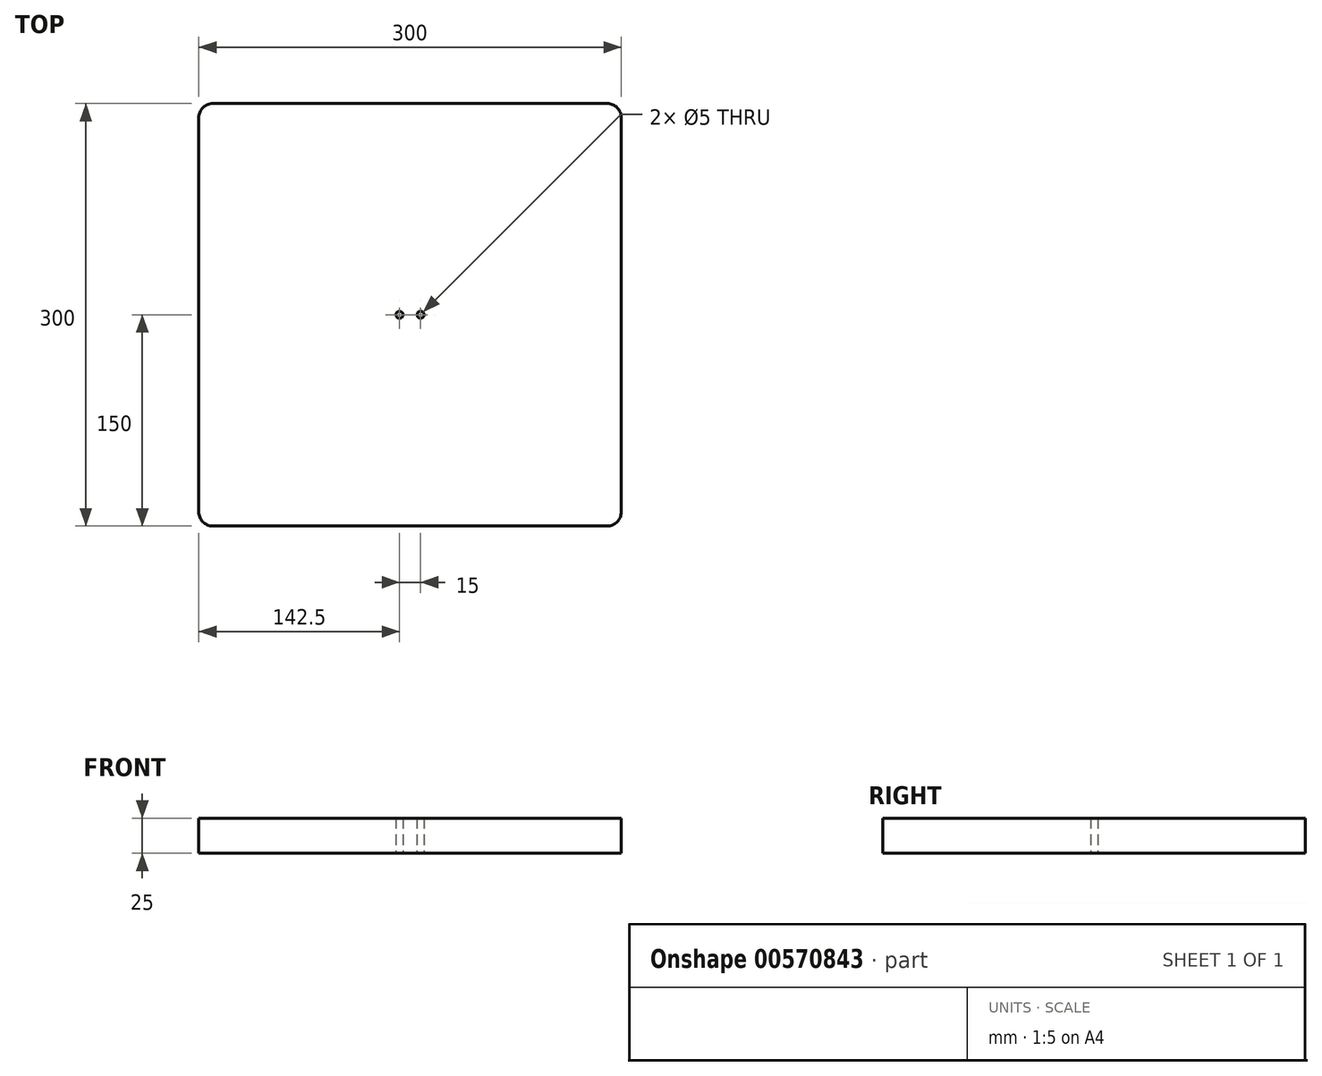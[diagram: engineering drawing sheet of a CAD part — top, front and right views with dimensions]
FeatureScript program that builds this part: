
annotation { "Feature Type Name" : "Feature", "Feature Type Description" : "" }
export const myFeature = defineFeature(function(context is Context, id is Id, definition is map)
    precondition{}
    {
        {
            var Q0;
            Q0=qCreatedBy(makeId("Top.planeOp"),FACE);
            var sketch = newSketch(context, id + "F0", { "sketchPlane" : qUnion([Q0])});
            skLineSegment(sketch, "E0.bottom", {"start": v(150, 150) * mm, "end": v(-150, 150) * mm});
            skLineSegment(sketch, "E0.top", {"start": v(150, -150) * mm, "end": v(-150, -150) * mm});
            skLineSegment(sketch, "E0.left", {"start": v(150, 150) * mm, "end": v(150, -150) * mm});
            skLineSegment(sketch, "E0.right", {"start": v(-150, 150) * mm, "end": v(-150, -150) * mm});
            skPoint(sketch, "E0.middle", {"position": v(0, 0) * mm});
            skCircle(sketch, "E1", {"center": v(-7.5, 0) * mm, "radius": 2.5 * mm});
            skCircle(sketch, "E2", {"center": v(7.5, 0) * mm, "radius": 2.5 * mm});
            skLineSegment(sketch, "E3", {"start": v(0, 150) * mm, "end": v(0, -150) * mm, "construction": true});
            skSolve(sketch);
        }
        {
            var Q0;
            Q0 = qSketchRegion(id + "F0", true);
            extrude(context, id + "F1", {"entities" : qUnion([Q0]), "depth" : 25 * mm, "offsetDistance" : 25 * mm});
        }
        {
            var Q0;
            Q0=makeQuery(id+"F1.opExtrude","SWEPT_EDGE",EDGE,{"disambiguationData":[OSD([sQuery(id+"F0.wireOp",EDGE,"E0.bottom"),sQuery(id+"F0.wireOp",EDGE,"E0.left")])]});
            var Q1;
            Q1=makeQuery(id+"F1.opExtrude","SWEPT_EDGE",EDGE,{"disambiguationData":[OSD([sQuery(id+"F0.wireOp",EDGE,"E0.bottom"),sQuery(id+"F0.wireOp",EDGE,"E0.right")])]});
            var Q2;
            Q2=makeQuery(id+"F1.opExtrude","SWEPT_EDGE",EDGE,{"disambiguationData":[OSD([sQuery(id+"F0.wireOp",EDGE,"E0.top"),sQuery(id+"F0.wireOp",EDGE,"E0.left")])]});
            var Q3;
            Q3=makeQuery(id+"F1.opExtrude","SWEPT_EDGE",EDGE,{"disambiguationData":[OSD([sQuery(id+"F0.wireOp",EDGE,"E0.top"),sQuery(id+"F0.wireOp",EDGE,"E0.right")])]});
            fillet(context, id + "F2", {"entities" : qUnion([Q0, Q1, Q2, Q3]), "radius" : 10 * mm, "tangentPropagation" : true, "allowEdgeOverflow" : false});
        }
    });
